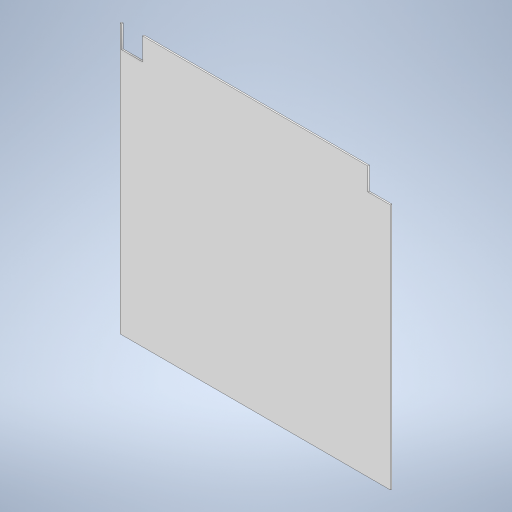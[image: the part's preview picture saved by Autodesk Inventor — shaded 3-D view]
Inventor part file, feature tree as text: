
AUTODESK INVENTOR PART (.ipt)
format: ipt  version: 2023 (Build 270158000, 158)  size: 209,408 bytes
history: native  units: mm
features: extrude x1
ambient origin geometry x8: Origin, YZ Plane, XZ Plane, XY Plane, X Axis, Y Axis, Z Axis, Center Point
bodies: Solid1 (feature_tree)
feature tree (1):
  extrude  "Extrusion1"  Depth=542.0mm
